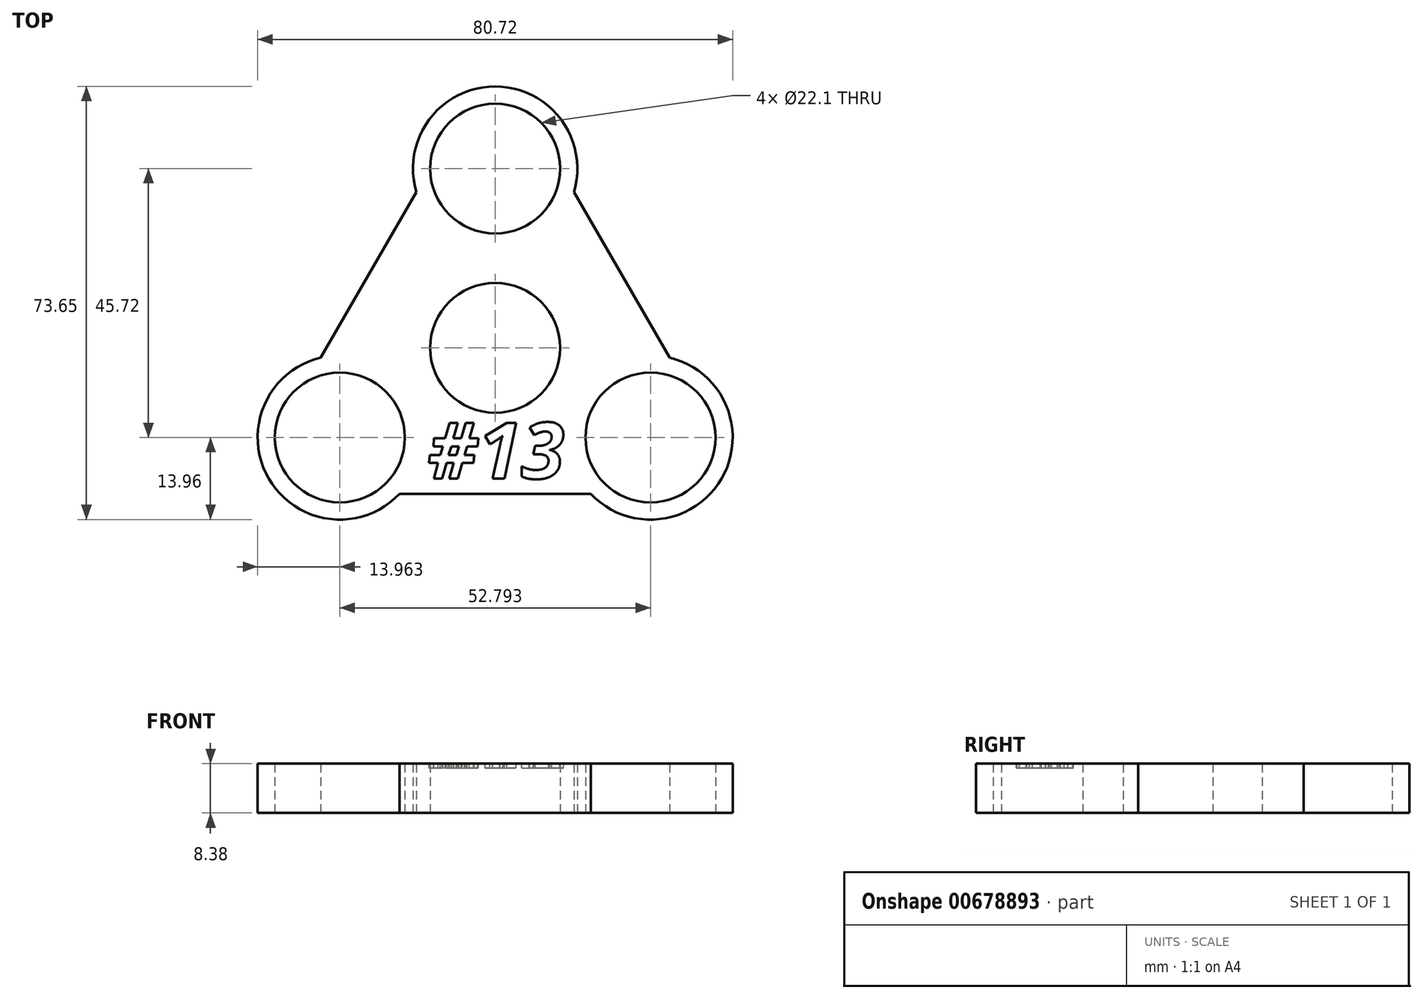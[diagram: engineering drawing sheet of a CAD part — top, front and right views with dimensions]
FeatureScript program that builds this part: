
annotation { "Feature Type Name" : "Feature", "Feature Type Description" : "" }
export const myFeature = defineFeature(function(context is Context, id is Id, definition is map)
    precondition{}
    {
        {
            var Q0;
            Q0=qCreatedBy(makeId("Top.planeOp"),FACE);
            var sketch = newSketch(context, id + "F0", { "sketchPlane" : qUnion([Q0])});
            skCircle(sketch, "E0", {"center": v(0, 0) * mm, "radius": 11.05 * mm});
            skLineSegment(sketch, "E1", {"start": v(0, 0) * mm, "end": v(0, 11.05) * mm});
            skCircle(sketch, "E2", {"center": v(0, 30.48) * mm, "radius": 11.05 * mm});
            skArc(sketch, "E3", {"start": v(13.39, 26.5) * mm, "mid": v(0, 44.45) * mm, "end": v(-13.39, 26.5) * mm});
            skCircle(sketch, "E4.1.0", {"center": v(-26.4, -15.24) * mm, "radius": 11.05 * mm});
            skCircle(sketch, "E4.2.0", {"center": v(26.4, -15.24) * mm, "radius": 11.05 * mm});
            skArc(sketch, "E5.1.0", {"start": v(-29.63, -1.64) * mm, "mid": v(-38.5, -22.21) * mm, "end": v(-16.25, -24.84) * mm});
            skLineSegment(sketch, "E6", {"start": v(-16.25, -24.84) * mm, "end": v(16.25, -24.84) * mm});
            skLineSegment(sketch, "E7.1.0", {"start": v(29.64, -1.65) * mm, "end": v(13.39, 26.5) * mm});
            skLineSegment(sketch, "E7.2.0", {"start": v(-13.39, 26.5) * mm, "end": v(-29.64, -1.65) * mm});
            skArc(sketch, "E8.trimOffspring", {"start": v(16.25, -24.84) * mm, "mid": v(38.5, -22.22) * mm, "end": v(29.63, -1.65) * mm});
            skSolve(sketch);
        }
        {
            var Q0;
            Q0 = qSketchRegion(id + "F0", true);
            extrude(context, id + "F1", {"entities" : qUnion([Q0]), "depth" : 8.38 * mm, "offsetDistance" : 25.4 * mm});
        }
        {
            var Q0;
            Q0=makeQuery(id+"F1.opExtrude","CAP_FACE",FACE,{"disambiguationData":[OSD([sQuery(id+"F0.wireOp",EDGE,"E0"),sQuery(id+"F0.wireOp",EDGE,"E2"),sQuery(id+"F0.wireOp",EDGE,"E3"),sQuery(id+"F0.wireOp",EDGE,"E4.1.0"),sQuery(id+"F0.wireOp",EDGE,"E4.2.0"),sQuery(id+"F0.wireOp",EDGE,"E5.1.0"),sQuery(id+"F0.wireOp",EDGE,"E6"),sQuery(id+"F0.wireOp",EDGE,"E7.1.0"),sQuery(id+"F0.wireOp",EDGE,"E7.2.0"),sQuery(id+"F0.wireOp",EDGE,"E8.trimOffspring")])],"isStart":false});
            var sketch = newSketch(context, id + "F2", { "sketchPlane" : qUnion([Q0])});
            skText(sketch, "E9", { "text": "#13", "fontName": "OpenSans-BoldItalic.ttf"});
            const initialGuessF2  = {"E9": [-0.0115, -0.02223, 1, 0, 0.00958]};
            skSetInitialGuess(sketch, initialGuessF2);
            skSolve(sketch);
        }
        {
            var Q0;
            Q0 = qSketchRegion(id + "F2", true);
            extrude(context, id + "F3", {"entities" : qUnion([Q0]), "operationType" : NewBodyOperationType.REMOVE, "oppositeDirection" : true, "depth" : 0.76 * mm, "offsetDistance" : 25.4 * mm});
        }
    });
